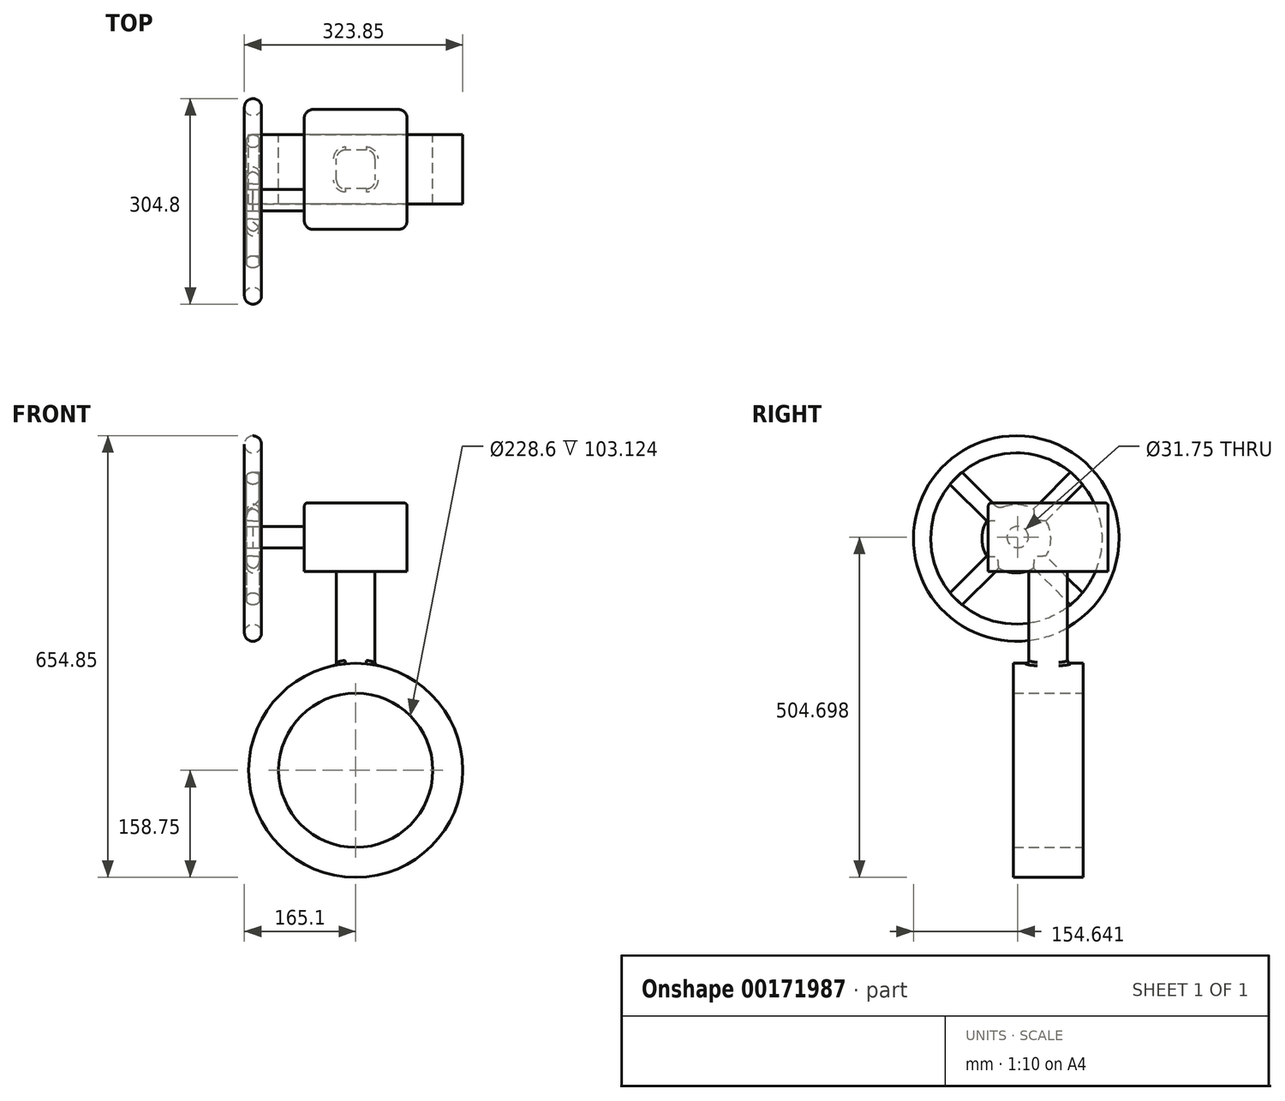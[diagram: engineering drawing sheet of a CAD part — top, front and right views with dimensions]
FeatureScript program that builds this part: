
annotation { "Feature Type Name" : "Feature", "Feature Type Description" : "" }
export const myFeature = defineFeature(function(context is Context, id is Id, definition is map)
    precondition{}
    {
        {
            var Q0;
            Q0=qCreatedBy(makeId("Front.planeOp"),FACE);
            var sketch = newSketch(context, id + "F0", { "sketchPlane" : qUnion([Q0])});
            skCircle(sketch, "E0", {"center": v(0, 0) * mm, "radius": 158.75 * mm});
            skSolve(sketch);
        }
        {
            var Q0;
            Q0=makeQuery(id+"F0.imprint","IMPRINT",FACE,{"disambiguationData":[TD([[makeQuery(id+"F0.imprint","IMPRINT",EDGE,{"derivedFrom":sQuery(id+"F0.wireOp",EDGE,"E0")}),1.0]])]});
            extrude(context, id + "F1", {"entities" : qUnion([Q0]), "endBound" : BoundingType.SYMMETRIC, "depth" : 103.12 * mm});
        }
        {
            var Q0;
            Q0=qCreatedBy(makeId("Top.planeOp"),FACE);
            cPlane(context, id + "F2", {"entities" : qUnion([Q0]), "cplaneType" : CPlaneType.OFFSET, "offset" : 152.4 * mm, "width" : 152.4 * mm, "height" : 152.4 * mm});
        }
        {
            var Q0;
            Q0=qCreatedBy(id+"F2.planeOp",FACE);
            var sketch = newSketch(context, id + "F3", { "sketchPlane" : qUnion([Q0])});
            skLineSegment(sketch, "E1.bottom", {"start": v(28.57, -28.58) * mm, "end": v(-28.58, -28.58) * mm});
            skLineSegment(sketch, "E1.top", {"start": v(28.57, 28.58) * mm, "end": v(-28.58, 28.57) * mm});
            skLineSegment(sketch, "E1.left", {"start": v(28.57, -28.57) * mm, "end": v(28.57, 28.58) * mm});
            skLineSegment(sketch, "E1.right", {"start": v(-28.58, -28.58) * mm, "end": v(-28.58, 28.57) * mm});
            skPoint(sketch, "E1.middle", {"position": v(0, 0) * mm});
            skSolve(sketch);
        }
        {
            var Q0;
            Q0=qSketchRegion(id+"F3",true);
            extrude(context, id + "F4", {"entities" : qUnion([Q0]), "operationType" : NewBodyOperationType.ADD, "depth" : 142.75 * mm});
        }
        {
            var Q0;
            Q0=makeQuery(id+"F4.opExtrude","CAP_FACE",FACE,{"disambiguationData":[OSD([sQuery(id+"F3.wireOp",EDGE,"E1.bottom"),sQuery(id+"F3.wireOp",EDGE,"E1.top"),sQuery(id+"F3.wireOp",EDGE,"E1.left"),sQuery(id+"F3.wireOp",EDGE,"E1.right")])],"isStart":false});
            var sketch = newSketch(context, id + "F5", { "sketchPlane" : qUnion([Q0])});
            skLineSegment(sketch, "E2.bottom", {"start": v(76.2, -88.9) * mm, "end": v(-76.2, -88.9) * mm});
            skLineSegment(sketch, "E2.top", {"start": v(76.2, 88.9) * mm, "end": v(-76.2, 88.9) * mm});
            skLineSegment(sketch, "E2.left", {"start": v(76.2, -88.9) * mm, "end": v(76.2, 88.9) * mm});
            skLineSegment(sketch, "E2.right", {"start": v(-76.2, -88.9) * mm, "end": v(-76.2, 88.9) * mm});
            skPoint(sketch, "E2.middle", {"position": v(0, 0) * mm});
            skSolve(sketch);
        }
        {
            var Q0;
            Q0=qSketchRegion(id+"F5",true);
            extrude(context, id + "F6", {"entities" : qUnion([Q0]), "operationType" : NewBodyOperationType.ADD, "depth" : 101.6 * mm});
        }
        {
            var Q0;
            Q0=makeQuery(id+"F6.opExtrude","SWEPT_FACE",FACE,{"disambiguationData":[OSD([sQuery(id+"F5.wireOp",EDGE,"E2.right")])]});
            var sketch = newSketch(context, id + "F7", { "sketchPlane" : qUnion([Q0])});
            skCircle(sketch, "E3", {"center": v(45.22, 345.95) * mm, "radius": 15.88 * mm});
            skPoint(sketch, "E3.centerSnap0", {"position": v(88.9, 345.95) * mm});
            skSolve(sketch);
        }
        {
            var Q0;
            Q0=qSketchRegion(id+"F7",true);
            extrude(context, id + "F8", {"entities" : qUnion([Q0]), "operationType" : NewBodyOperationType.ADD, "depth" : 76.2 * mm});
        }
        {
            var Q0;
            Q0=makeQuery(id+"F8.opExtrude","CAP_FACE",FACE,{"disambiguationData":[OSD([sQuery(id+"F7.wireOp",EDGE,"E3")])],"isStart":false});
            var sketch = newSketch(context, id + "F9", { "sketchPlane" : qUnion([Q0])});
            skCircle(sketch, "E4", {"center": v(47.46, 343.7) * mm, "radius": 152.4 * mm});
            skArc(sketch, "E5", {"start": v(73.26, 387.46) * mm, "mid": v(47.46, 394.5) * mm, "end": v(21.66, 387.46) * mm});
            skCircle(sketch, "E6", {"center": v(47.46, 343.7) * mm, "radius": 127 * mm});
            skLineSegment(sketch, "E7.trimOffspring", {"start": v(91.22, 317.9) * mm, "end": v(145.8, 263.33) * mm});
            skLineSegment(sketch, "E8.trimOffspring", {"start": v(73.26, 299.94) * mm, "end": v(127.84, 245.37) * mm});
            skLineSegment(sketch, "E9.trimOffspring", {"start": v(21.66, 299.94) * mm, "end": v(-32.9, 245.37) * mm});
            skLineSegment(sketch, "E10.trimOffspring", {"start": v(3.7, 317.9) * mm, "end": v(-50.87, 263.33) * mm});
            skLineSegment(sketch, "E11.trimOffspring", {"start": v(3.7, 369.5) * mm, "end": v(-50.87, 424.08) * mm});
            skLineSegment(sketch, "E12.trimOffspring", {"start": v(21.66, 387.46) * mm, "end": v(-32.9, 442.04) * mm});
            skLineSegment(sketch, "E13.trimOffspring", {"start": v(73.26, 387.46) * mm, "end": v(127.84, 442.04) * mm});
            skLineSegment(sketch, "E14.trimOffspring", {"start": v(91.22, 369.5) * mm, "end": v(145.8, 424.08) * mm});
            skArc(sketch, "E15.trimOffspring", {"start": v(91.22, 317.9) * mm, "mid": v(98.26, 343.7) * mm, "end": v(91.22, 369.5) * mm});
            skArc(sketch, "E16.trimOffspring", {"start": v(21.66, 299.94) * mm, "mid": v(47.46, 292.9) * mm, "end": v(73.26, 299.94) * mm});
            skArc(sketch, "E17.trimOffspring", {"start": v(3.7, 369.5) * mm, "mid": v(-3.34, 343.7) * mm, "end": v(3.7, 317.9) * mm});
            skSolve(sketch);
        }
        {
            var Q0;
            Q0=qSketchRegion(id+"F9",true);
            extrude(context, id + "F10", {"entities" : qUnion([Q0]), "endBound" : BoundingType.SYMMETRIC, "depth" : 25.4 * mm});
        }
        {
            var Q0;
            Q0=makeQuery(id+"F9.imprint","IMPRINT",FACE,{"disambiguationData":[TD([[makeQuery(id+"F9.imprint","IMPRINT",EDGE,{"derivedFrom":sQuery(id+"F9.wireOp",EDGE,"E5")}),1.0]])]});
            extrude(context, id + "F11", {"entities" : qUnion([Q0]), "endBound" : BoundingType.SYMMETRIC, "depth" : 19.05 * mm});
        }
        {
            var Q0;
            Q0=makeQuery(id+"F10.opExtrude","CAP_EDGE",EDGE,{"disambiguationData":[OSD([sQuery(id+"F9.wireOp",EDGE,"E6")])],"isStart":false});
            var Q1;
            Q1=makeQuery(id+"F10.opExtrude","CAP_EDGE",EDGE,{"disambiguationData":[OSD([sQuery(id+"F9.wireOp",EDGE,"E4")])],"isStart":false});
            var Q2;
            Q2=makeQuery(id+"F10.opExtrude","CAP_EDGE",EDGE,{"disambiguationData":[OSD([sQuery(id+"F9.wireOp",EDGE,"E4")])],"isStart":true});
            var Q3;
            Q3=makeQuery(id+"F10.opExtrude","CAP_EDGE",EDGE,{"disambiguationData":[OSD([sQuery(id+"F9.wireOp",EDGE,"E6")])],"isStart":true});
            fillet(context, id + "F12", {"entities" : qUnion([Q0, Q1, Q2, Q3]), "radius" : 12.7 * mm, "tangentPropagation" : true, "allowEdgeOverflow" : false});
        }
        {
            var Q0;
            Q0=makeQuery(id+"F11.opExtrude","CAP_EDGE",EDGE,{"disambiguationData":[OSD([sQuery(id+"F9.wireOp",EDGE,"E12.trimOffspring")])],"isStart":false});
            var Q1;
            Q1=makeQuery(id+"F11.opExtrude","CAP_EDGE",EDGE,{"disambiguationData":[OSD([sQuery(id+"F9.wireOp",EDGE,"E5")])],"isStart":false});
            var Q2;
            Q2=makeQuery(id+"F11.opExtrude","CAP_EDGE",EDGE,{"disambiguationData":[OSD([sQuery(id+"F9.wireOp",EDGE,"E13.trimOffspring")])],"isStart":false});
            var Q3;
            Q3=makeQuery(id+"F11.opExtrude","CAP_EDGE",EDGE,{"disambiguationData":[OSD([sQuery(id+"F9.wireOp",EDGE,"E11.trimOffspring")])],"isStart":false});
            var Q4;
            Q4=makeQuery(id+"F11.opExtrude","CAP_EDGE",EDGE,{"disambiguationData":[OSD([sQuery(id+"F9.wireOp",EDGE,"E17.trimOffspring")])],"isStart":false});
            var Q5;
            Q5=makeQuery(id+"F11.opExtrude","CAP_EDGE",EDGE,{"disambiguationData":[OSD([sQuery(id+"F9.wireOp",EDGE,"E10.trimOffspring")])],"isStart":false});
            var Q6;
            Q6=makeQuery(id+"F11.opExtrude","CAP_EDGE",EDGE,{"disambiguationData":[OSD([sQuery(id+"F9.wireOp",EDGE,"E14.trimOffspring")])],"isStart":false});
            var Q7;
            Q7=makeQuery(id+"F11.opExtrude","CAP_EDGE",EDGE,{"disambiguationData":[OSD([sQuery(id+"F9.wireOp",EDGE,"E15.trimOffspring")])],"isStart":false});
            var Q8;
            Q8=makeQuery(id+"F11.opExtrude","CAP_EDGE",EDGE,{"disambiguationData":[OSD([sQuery(id+"F9.wireOp",EDGE,"E7.trimOffspring")])],"isStart":false});
            var Q9;
            Q9=makeQuery(id+"F11.opExtrude","CAP_EDGE",EDGE,{"disambiguationData":[OSD([sQuery(id+"F9.wireOp",EDGE,"E8.trimOffspring")])],"isStart":false});
            var Q10;
            Q10=makeQuery(id+"F11.opExtrude","CAP_EDGE",EDGE,{"disambiguationData":[OSD([sQuery(id+"F9.wireOp",EDGE,"E16.trimOffspring")])],"isStart":false});
            var Q11;
            Q11=makeQuery(id+"F11.opExtrude","CAP_EDGE",EDGE,{"disambiguationData":[OSD([sQuery(id+"F9.wireOp",EDGE,"E9.trimOffspring")])],"isStart":false});
            var Q12;
            Q12=makeQuery(id+"F11.opExtrude","CAP_EDGE",EDGE,{"disambiguationData":[OSD([sQuery(id+"F9.wireOp",EDGE,"E14.trimOffspring")])],"isStart":true});
            var Q13;
            Q13=makeQuery(id+"F11.opExtrude","SWEPT_EDGE",EDGE,{"disambiguationData":[OSD([sQuery(id+"F9.wireOp",EDGE,"E5"),sQuery(id+"F9.wireOp",EDGE,"E13.trimOffspring")])]});
            var Q14;
            Q14=makeQuery(id+"F11.opExtrude","CAP_EDGE",EDGE,{"disambiguationData":[OSD([sQuery(id+"F9.wireOp",EDGE,"E11.trimOffspring")])],"isStart":true});
            var Q15;
            Q15=makeQuery(id+"F11.opExtrude","CAP_EDGE",EDGE,{"disambiguationData":[OSD([sQuery(id+"F9.wireOp",EDGE,"E12.trimOffspring")])],"isStart":true});
            var Q16;
            Q16=makeQuery(id+"F11.opExtrude","CAP_EDGE",EDGE,{"disambiguationData":[OSD([sQuery(id+"F9.wireOp",EDGE,"E5")])],"isStart":true});
            var Q17;
            Q17=makeQuery(id+"F11.opExtrude","CAP_EDGE",EDGE,{"disambiguationData":[OSD([sQuery(id+"F9.wireOp",EDGE,"E15.trimOffspring")])],"isStart":true});
            var Q18;
            Q18=makeQuery(id+"F11.opExtrude","CAP_EDGE",EDGE,{"disambiguationData":[OSD([sQuery(id+"F9.wireOp",EDGE,"E7.trimOffspring")])],"isStart":true});
            var Q19;
            Q19=makeQuery(id+"F11.opExtrude","CAP_EDGE",EDGE,{"disambiguationData":[OSD([sQuery(id+"F9.wireOp",EDGE,"E8.trimOffspring")])],"isStart":true});
            var Q20;
            Q20=makeQuery(id+"F11.opExtrude","CAP_EDGE",EDGE,{"disambiguationData":[OSD([sQuery(id+"F9.wireOp",EDGE,"E16.trimOffspring")])],"isStart":true});
            var Q21;
            Q21=makeQuery(id+"F11.opExtrude","CAP_EDGE",EDGE,{"disambiguationData":[OSD([sQuery(id+"F9.wireOp",EDGE,"E17.trimOffspring")])],"isStart":true});
            var Q22;
            Q22=makeQuery(id+"F11.opExtrude","CAP_EDGE",EDGE,{"disambiguationData":[OSD([sQuery(id+"F9.wireOp",EDGE,"E10.trimOffspring")])],"isStart":true});
            var Q23;
            Q23=makeQuery(id+"F11.opExtrude","CAP_EDGE",EDGE,{"disambiguationData":[OSD([sQuery(id+"F9.wireOp",EDGE,"E9.trimOffspring")])],"isStart":true});
            fillet(context, id + "F13", {"entities" : qUnion([Q0, Q1, Q2, Q3, Q4, Q5, Q6, Q7, Q8, Q9, Q10, Q11, Q12, Q13, Q14, Q15, Q16, Q17, Q18, Q19, Q20, Q21, Q22, Q23]), "radius" : 9.52 * mm, "tangentPropagation" : true, "allowEdgeOverflow" : false});
        }
        {
            var Q0;
            Q0=makeQuery(id+"F1.opExtrude","CAP_FACE",FACE,{"disambiguationData":[OSD([sQuery(id+"F0.wireOp",EDGE,"E0")])],"isStart":true});
            var sketch = newSketch(context, id + "F14", { "sketchPlane" : qUnion([Q0])});
            skCircle(sketch, "E18", {"center": v(0, 0) * mm, "radius": 114.3 * mm});
            skSolve(sketch);
        }
        {
            var Q0;
            Q0=qSketchRegion(id+"F14",true);
            extrude(context, id + "F15", {"entities" : qUnion([Q0]), "operationType" : NewBodyOperationType.REMOVE, "endBound" : BoundingType.THROUGH_ALL, "oppositeDirection" : true, "depth" : 25.4 * mm});
        }
        {
            var Q0;
            Q0=makeQuery(id+"F4.opExtrude","SWEPT_EDGE",EDGE,{"disambiguationData":[OSD([sQuery(id+"F3.wireOp",EDGE,"E1.top"),sQuery(id+"F3.wireOp",EDGE,"E1.left")])]});
            var Q1;
            Q1=makeQuery(id+"F4.opExtrude","SWEPT_EDGE",EDGE,{"disambiguationData":[OSD([sQuery(id+"F3.wireOp",EDGE,"E1.top"),sQuery(id+"F3.wireOp",EDGE,"E1.right")])]});
            var Q2;
            Q2=makeQuery(id+"F4.opExtrude","SWEPT_EDGE",EDGE,{"disambiguationData":[OSD([sQuery(id+"F3.wireOp",EDGE,"E1.bottom"),sQuery(id+"F3.wireOp",EDGE,"E1.left")])]});
            var Q3;
            Q3=makeQuery(id+"F4.opExtrude","SWEPT_EDGE",EDGE,{"disambiguationData":[OSD([sQuery(id+"F3.wireOp",EDGE,"E1.bottom"),sQuery(id+"F3.wireOp",EDGE,"E1.right")])]});
            var Q4;
            Q4=makeQuery(id+"F6.opExtrude","SWEPT_EDGE",EDGE,{"disambiguationData":[OSD([sQuery(id+"F5.wireOp",EDGE,"E2.bottom"),sQuery(id+"F5.wireOp",EDGE,"E2.right")])]});
            var Q5;
            Q5=makeQuery(id+"F6.opExtrude","SWEPT_EDGE",EDGE,{"disambiguationData":[OSD([sQuery(id+"F5.wireOp",EDGE,"E2.bottom"),sQuery(id+"F5.wireOp",EDGE,"E2.left")])]});
            var Q6;
            Q6=makeQuery(id+"F6.opExtrude","SWEPT_EDGE",EDGE,{"disambiguationData":[OSD([sQuery(id+"F5.wireOp",EDGE,"E2.top"),sQuery(id+"F5.wireOp",EDGE,"E2.right")])]});
            var Q7;
            Q7=makeQuery(id+"F6.opExtrude","SWEPT_EDGE",EDGE,{"disambiguationData":[OSD([sQuery(id+"F5.wireOp",EDGE,"E2.top"),sQuery(id+"F5.wireOp",EDGE,"E2.left")])]});
            fillet(context, id + "F16", {"entities" : qUnion([Q0, Q1, Q2, Q3, Q4, Q5, Q6, Q7]), "radius" : 12.7 * mm, "tangentPropagation" : true, "allowEdgeOverflow" : false});
        }
        {
            var Q0;
            Q0=makeQuery(id+"F6.opExtrude","CAP_EDGE",EDGE,{"disambiguationData":[OSD([sQuery(id+"F5.wireOp",EDGE,"E2.top")])],"isStart":false});
            fillet(context, id + "F17", {"entities" : qUnion([Q0]), "radius" : 5.08 * mm, "tangentPropagation" : true, "allowEdgeOverflow" : false});
        }
        {
            var Q0;
            Q0=makeQuery(id+"F4.boolean.opBoolean","INTERSECT",EDGE,{"derivedFrom":[makeQuery(id+"F1.opExtrude","SWEPT_FACE",FACE,{"disambiguationData":[OSD([sQuery(id+"F0.wireOp",EDGE,"E0")])]}),makeQuery(id+"F4.opExtrude","SWEPT_FACE",FACE,{"disambiguationData":[OSD([sQuery(id+"F3.wireOp",EDGE,"E1.bottom")])]})]});
            fillet(context, id + "F18", {"entities" : qUnion([Q0]), "radius" : 5.08 * mm, "tangentPropagation" : true, "allowEdgeOverflow" : false});
        }
    });
